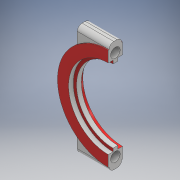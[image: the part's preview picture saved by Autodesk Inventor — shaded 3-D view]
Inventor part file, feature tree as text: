
AUTODESK INVENTOR PART (.ipt)
format: ipt  version: 2017 (Build 210142000, 142)  size: 185,344 bytes
history: native  units: mm
features: extrude x4, sketch x2
ambient origin geometry x8: Origin, YZ Plane, XZ Plane, XY Plane, X Axis, Y Axis, Z Axis, Center Point
bodies: Solid1 (feature_tree)
feature tree (6):
  sketch  "Sketch1"  dims[d0=32.0mm d1=23.0mm d2=0.0mm d3=0.0mm d4=25.0mm d5=0.0mm d6=16.0mm d7=0.0mm d8=16.0mm]
  extrude  "Extrusion1"  Depth=16.0mm
  extrude  "Extrusion2"  Depth=1.5mm TaperAngle=0.0deg
  sketch  "Sketch3"  dims[d9=4.5mm d10=0.0mm d11=1.5mm d12=0.0mm d13=3.0mm d14=5.0mm d15=2.7mm d16=2.7mm d17=90.0deg d18=90.0deg d19=90.0deg d20=6.0mm d21=2.75mm d22=1.25mm d23=1.0mm d24=0.0mm d25=24.0mm d26=27.5mm d27=29.0mm d28=1.5mm d29=3.0mm d30=25.75mm d31=0.75mm d32=1.5mm d33=1.5mm d34=24.0mm d35=0.75mm d36=2.75mm d37=1.25mm d38=10.0mm d39=0.0mm d40=10.0mm d41=0.0mm]
  extrude  "Extrusion3"  Depth=10.0mm TaperAngle=0.0deg
  extrude  "Extrusion4"  Depth=10.0mm TaperAngle=0.0deg
